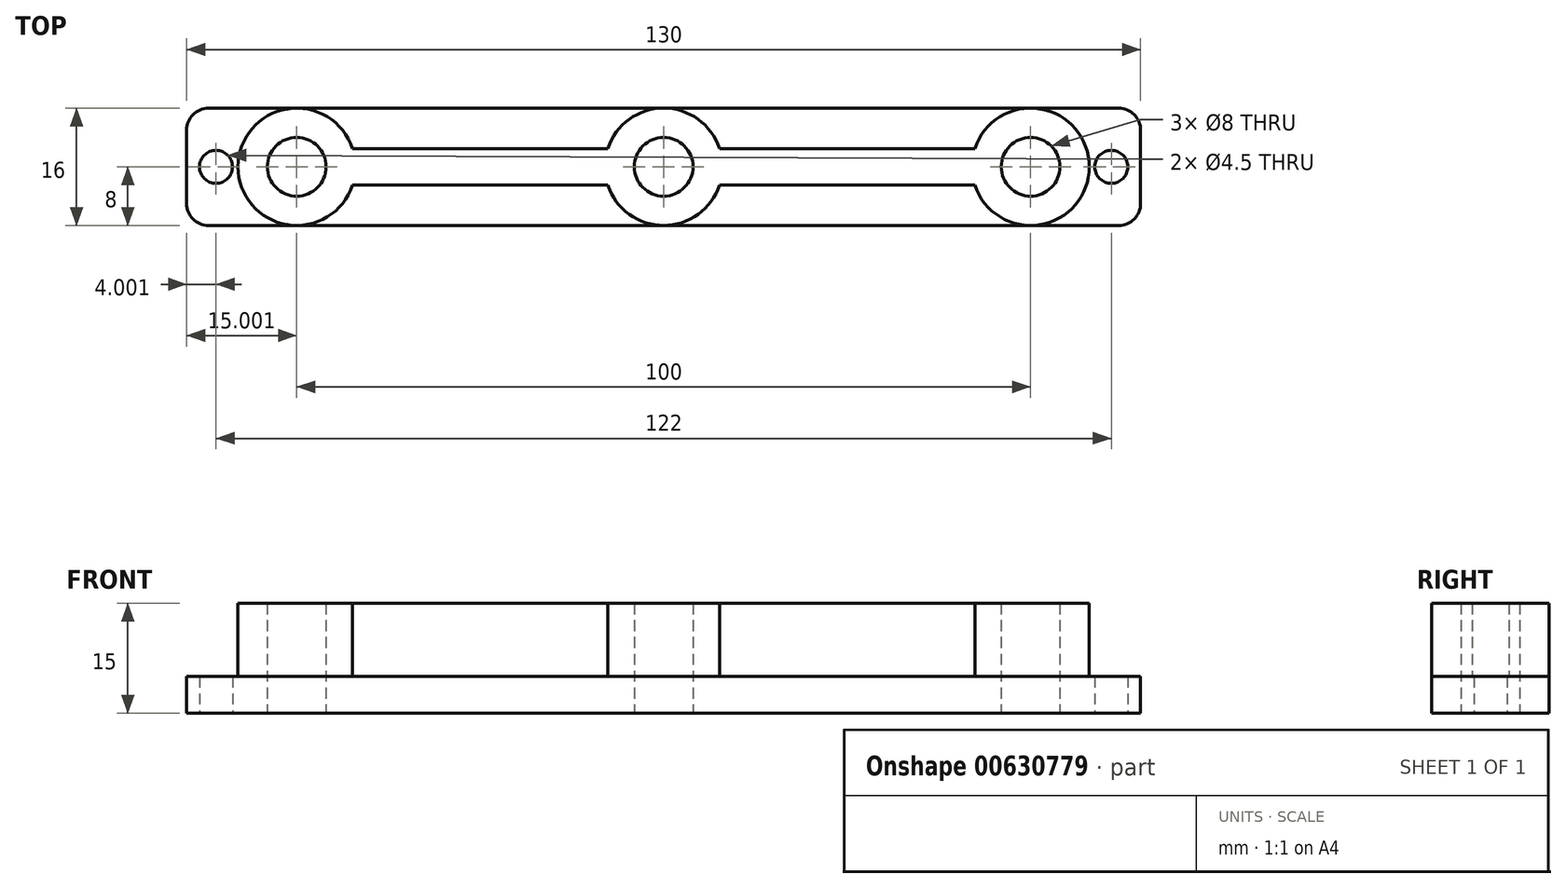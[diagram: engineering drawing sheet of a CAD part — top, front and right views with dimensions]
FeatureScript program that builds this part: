
annotation { "Feature Type Name" : "Feature", "Feature Type Description" : "" }
export const myFeature = defineFeature(function(context is Context, id is Id, definition is map)
    precondition{}
    {
        {
            var Q0;
            Q0=qCreatedBy(makeId("Top.planeOp"),FACE);
            var sketch = newSketch(context, id + "F0", { "sketchPlane" : qUnion([Q0])});
            skCircle(sketch, "E0", {"center": v(-21.69, 0) * mm, "radius": 4 * mm});
            skCircle(sketch, "E1", {"center": v(-21.69, 0) * mm, "radius": 8 * mm});
            skCircle(sketch, "E2", {"center": v(78.31, 0) * mm, "radius": 4 * mm});
            skCircle(sketch, "E3", {"center": v(78.31, 0) * mm, "radius": 8 * mm});
            skLineSegment(sketch, "E4.bottom", {"start": v(-33.69, 8) * mm, "end": v(90.31, 8) * mm});
            skLineSegment(sketch, "E4.top", {"start": v(-33.69, -8) * mm, "end": v(90.31, -8) * mm});
            skLineSegment(sketch, "E4.left", {"start": v(-36.69, 5) * mm, "end": v(-36.69, -5) * mm});
            skLineSegment(sketch, "E4.right", {"start": v(93.31, 5) * mm, "end": v(93.31, -5) * mm});
            skCircle(sketch, "E5", {"center": v(-32.69, 0) * mm, "radius": 2.25 * mm});
            skCircle(sketch, "E6", {"center": v(89.31, 0) * mm, "radius": 2.25 * mm});
            skPoint(sketch, "E7.visualSharp", {"position": v(93.31, 8) * mm});
            skArc(sketch, "E7.filletArc", {"start": v(93.31, 5) * mm, "mid": v(92.43, 7.12) * mm, "end": v(90.31, 8) * mm});
            skPoint(sketch, "E8.visualSharp", {"position": v(93.31, -8) * mm});
            skArc(sketch, "E8.filletArc", {"start": v(90.31, -8) * mm, "mid": v(92.43, -7.12) * mm, "end": v(93.31, -5) * mm});
            skPoint(sketch, "E9.visualSharp", {"position": v(-36.69, -8) * mm});
            skArc(sketch, "E9.filletArc", {"start": v(-36.69, -5) * mm, "mid": v(-35.81, -7.12) * mm, "end": v(-33.69, -8) * mm});
            skPoint(sketch, "E10.visualSharp", {"position": v(-36.69, 8) * mm});
            skArc(sketch, "E10.filletArc", {"start": v(-33.69, 8) * mm, "mid": v(-35.81, 7.12) * mm, "end": v(-36.69, 5) * mm});
            skPoint(sketch, "E11.center.orphan", {"position": v(-10.69, 0) * mm});
            skPoint(sketch, "E12.center.orphan", {"position": v(67.31, 0) * mm});
            skLineSegment(sketch, "E13.bottom", {"start": v(-14.09, 2.5) * mm, "end": v(20.71, 2.5) * mm});
            skLineSegment(sketch, "E13.top", {"start": v(-15.49, -2.5) * mm, "end": v(20.71, -2.5) * mm});
            skLineSegment(sketch, "E13.left", {"start": v(-14.09, 2.58) * mm, "end": v(-14.09, 2.5) * mm});
            skCircle(sketch, "E14", {"center": v(28.31, 0) * mm, "radius": 4 * mm});
            skCircle(sketch, "E15", {"center": v(28.31, 0) * mm, "radius": 8 * mm});
            skLineSegment(sketch, "E16.trimOffspring", {"start": v(35.91, 2.5) * mm, "end": v(70.71, 2.5) * mm});
            skLineSegment(sketch, "E17.trimOffspring", {"start": v(35.91, -2.5) * mm, "end": v(70.71, -2.5) * mm});
            skSolve(sketch);
        }
        {
            var Q0;
            {var subQ0=sQuery(id+"F0.wireOp",EDGE,"E13.top");Q0=makeQuery(id+"F0.imprint","IMPRINT",FACE,{"disambiguationData":[TD([[makeQuery(id+"F0.imprint","IMPRINT",EDGE,{"derivedFrom":subQ0}),-1.0]])]});}
            var Q1;
            {var subQ0=sQuery(id+"F0.wireOp",EDGE,"E13.bottom");Q1=makeQuery(id+"F0.imprint","IMPRINT",FACE,{"disambiguationData":[TD([[makeQuery(id+"F0.imprint","IMPRINT",EDGE,{"derivedFrom":subQ0}),1.0]])]});}
            var Q2;
            Q2=makeQuery(id+"F0.imprint","IMPRINT",FACE,{"disambiguationData":[TD([[makeQuery(id+"F0.imprint","IMPRINT",EDGE,{"derivedFrom":sQuery(id+"F0.wireOp",EDGE,"E4.left")}),1.0]])]});
            var Q3;
            Q3=makeQuery(id+"F0.imprint","IMPRINT",FACE,{"disambiguationData":[TD([[makeQuery(id+"F0.imprint","IMPRINT",EDGE,{"derivedFrom":sQuery(id+"F0.wireOp",EDGE,"E4.right")}),-1.0]])]});
            var Q4;
            {var subQ0=sQuery(id+"F0.wireOp",EDGE,"E16.trimOffspring");Q4=makeQuery(id+"F0.imprint","IMPRINT",FACE,{"disambiguationData":[TD([[makeQuery(id+"F0.imprint","IMPRINT",EDGE,{"derivedFrom":subQ0}),1.0]])]});}
            var Q5;
            {var subQ0=sQuery(id+"F0.wireOp",EDGE,"E17.trimOffspring");Q5=makeQuery(id+"F0.imprint","IMPRINT",FACE,{"disambiguationData":[TD([[makeQuery(id+"F0.imprint","IMPRINT",EDGE,{"derivedFrom":subQ0}),-1.0]])]});}
            extrude(context, id + "F1", {"entities" : qUnion([Q0, Q1, Q2, Q3, Q4, Q5]), "depth" : 5 * mm, "offsetDistance" : 25 * mm});
        }
        {
            var Q0;
            Q0=makeQuery(id+"F0.imprint","IMPRINT",FACE,{"disambiguationData":[TD([[makeQuery(id+"F0.imprint","IMPRINT",EDGE,{"derivedFrom":sQuery(id+"F0.wireOp",EDGE,"E0")}),-1.0]])]});
            var Q1;
            Q1=makeQuery(id+"F0.imprint","IMPRINT",FACE,{"disambiguationData":[TD([[makeQuery(id+"F0.imprint","IMPRINT",EDGE,{"derivedFrom":sQuery(id+"F0.wireOp",EDGE,"E2")}),-1.0]])]});
            var Q2;
            {var subQ1=sQuery(id+"F0.wireOp",EDGE,"E13.bottom");Q2=makeQuery(id+"F0.imprint","IMPRINT",FACE,{"disambiguationData":[TD([[makeQuery(id+"F0.imprint","IMPRINT",EDGE,{"derivedFrom":subQ1}),-1.0]])]});}
            var Q3;
            {var subQ0=sQuery(id+"F0.wireOp",EDGE,"E16.trimOffspring");Q3=makeQuery(id+"F0.imprint","IMPRINT",FACE,{"disambiguationData":[TD([[makeQuery(id+"F0.imprint","IMPRINT",EDGE,{"derivedFrom":subQ0}),-1.0]])]});}
            var Q4;
            Q4=makeQuery(id+"F0.imprint","IMPRINT",FACE,{"disambiguationData":[TD([[makeQuery(id+"F0.imprint","IMPRINT",EDGE,{"derivedFrom":sQuery(id+"F0.wireOp",EDGE,"E14")}),-1.0]])]});
            extrude(context, id + "F2", {"entities" : qUnion([Q0, Q1, Q2, Q3, Q4]), "operationType" : NewBodyOperationType.ADD, "depth" : 15 * mm, "offsetDistance" : 25 * mm});
        }
    });
